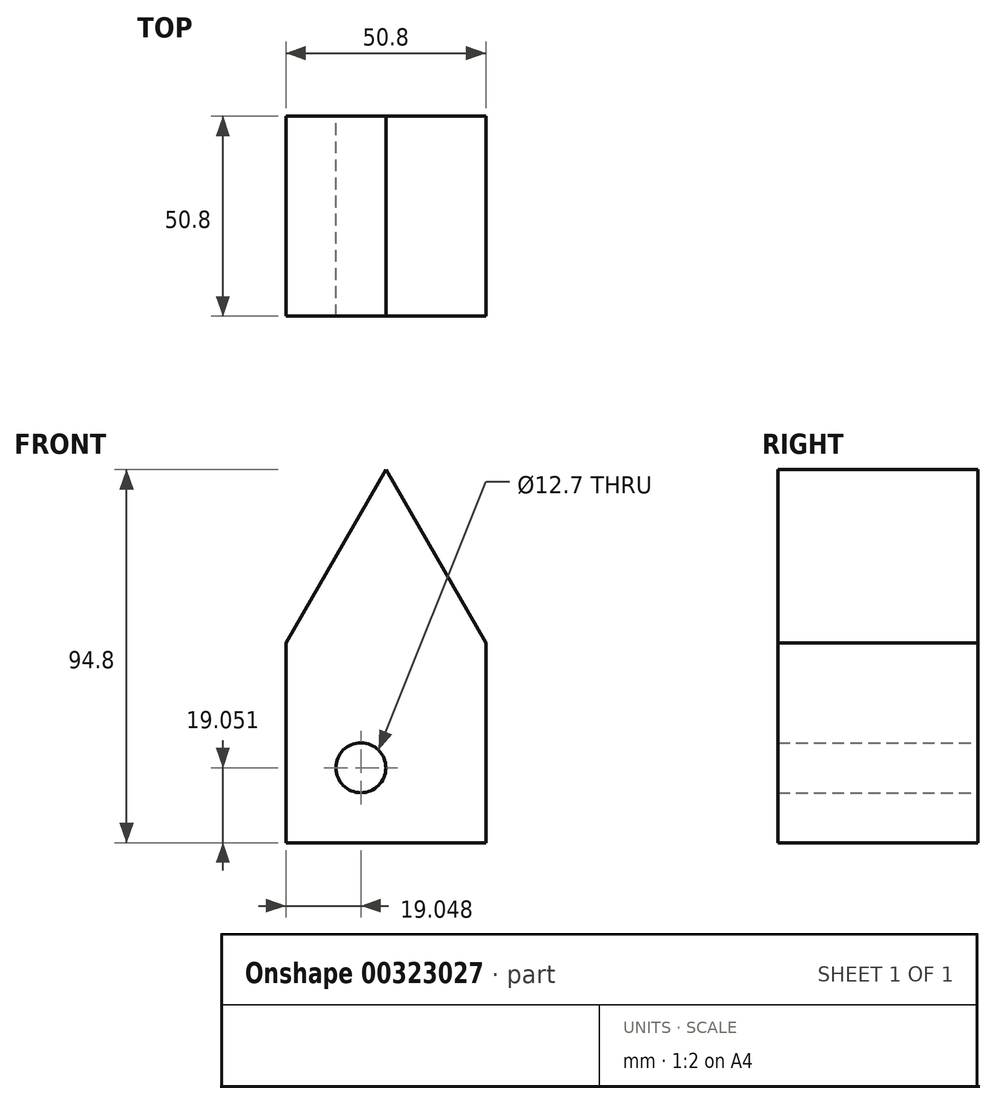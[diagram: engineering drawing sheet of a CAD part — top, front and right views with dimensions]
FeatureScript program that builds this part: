
annotation { "Feature Type Name" : "Feature", "Feature Type Description" : "" }
export const myFeature = defineFeature(function(context is Context, id is Id, definition is map)
    precondition{}
    {
        {
            var Q0;
            Q0=qCreatedBy(makeId("Front.planeOp"),FACE);
            var sketch = newSketch(context, id + "F0", { "sketchPlane" : qUnion([Q0])});
            skLineSegment(sketch, "E0.top", {"start": v(-24.9, -20.88) * mm, "end": v(25.9, -20.88) * mm});
            skLineSegment(sketch, "E0.left", {"start": v(-24.9, 29.92) * mm, "end": v(-24.9, -20.88) * mm});
            skLineSegment(sketch, "E0.right", {"start": v(25.9, 29.92) * mm, "end": v(25.9, -20.88) * mm});
            skLineSegment(sketch, "E1", {"start": v(-24.9, 29.92) * mm, "end": v(0.5, 73.92) * mm});
            skLineSegment(sketch, "E2", {"start": v(0.5, 73.92) * mm, "end": v(25.9, 29.92) * mm});
            skCircle(sketch, "E3", {"center": v(-5.84, -1.83) * mm, "radius": 6.35 * mm});
            skSolve(sketch);
        }
        {
            var Q0;
            Q0 = qSketchRegion(id + "F0", true);
            extrude(context, id + "F1", {"entities" : qUnion([Q0]), "depth" : 50.8 * mm});
        }
    });
